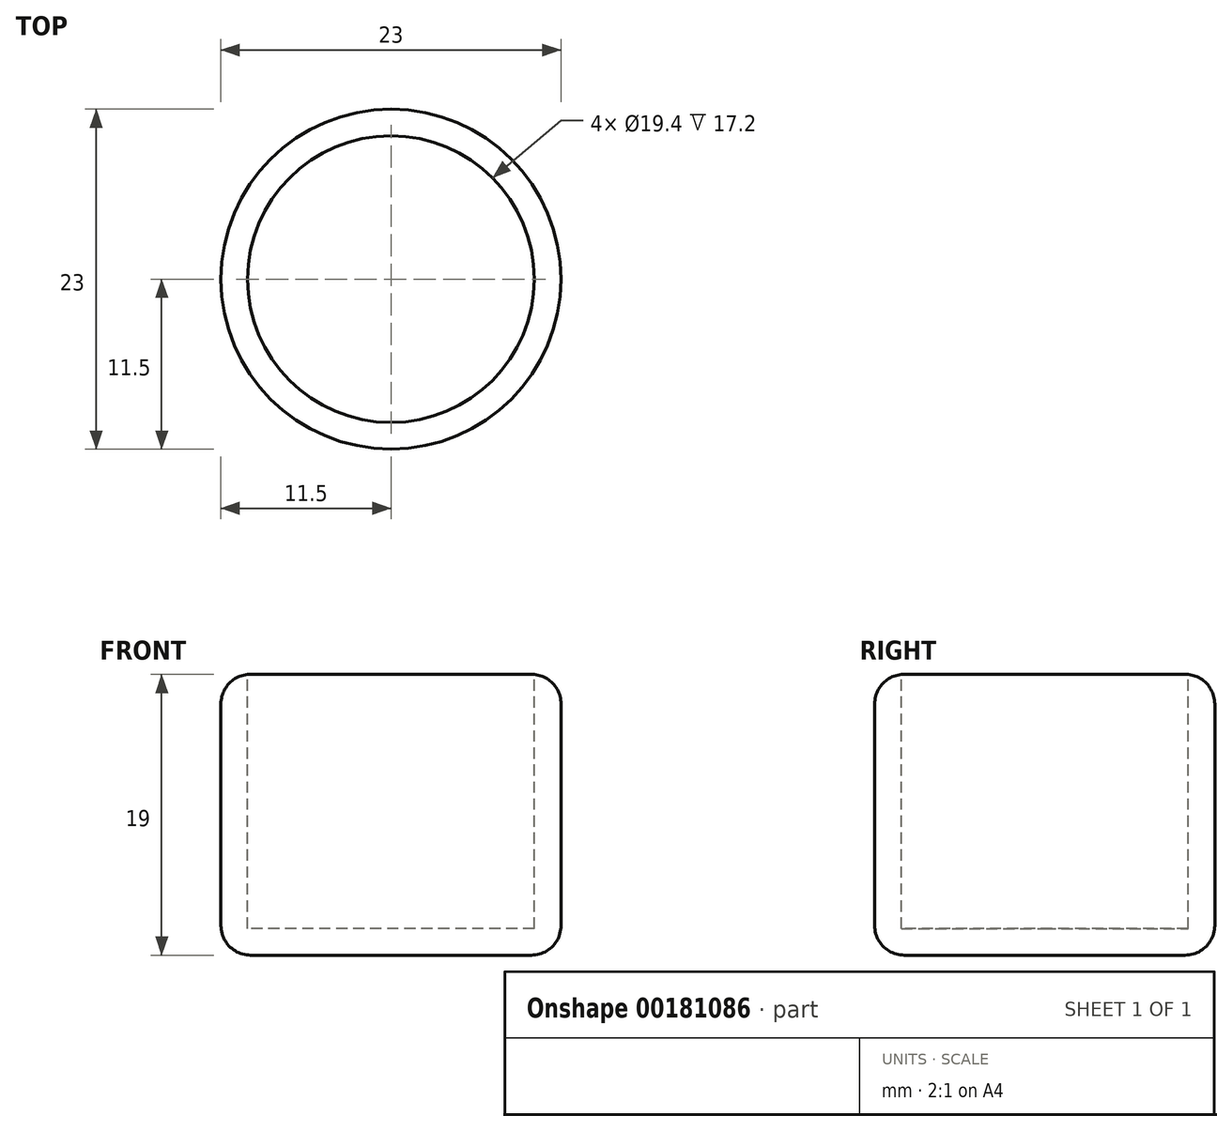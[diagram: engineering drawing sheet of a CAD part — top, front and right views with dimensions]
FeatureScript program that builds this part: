
annotation { "Feature Type Name" : "Feature", "Feature Type Description" : "" }
export const myFeature = defineFeature(function(context is Context, id is Id, definition is map)
    precondition{}
    {
        {
            var Q0;
            Q0=qCreatedBy(makeId("Top.planeOp"),FACE);
            var sketch = newSketch(context, id + "F0", { "sketchPlane" : qUnion([Q0])});
            skCircle(sketch, "E0", {"center": v(0, 0) * mm, "radius": 11.5 * mm});
            skSolve(sketch);
        }
        {
            var Q0;
            Q0=makeQuery(id+"F0.imprint","IMPRINT",FACE,{"disambiguationData":[TD([[makeQuery(id+"F0.imprint","IMPRINT",EDGE,{"derivedFrom":sQuery(id+"F0.wireOp",EDGE,"E0")}),1.0]])]});
            var Q1;
            Q1=sQuery(id+"F0.wireOp",EDGE,"E0");
            extrude(context, id + "F1", {"entities" : qUnion([Q0]), "surfaceEntities" : qUnion([Q1]), "oppositeDirection" : true, "depth" : 19 * mm});
        }
        {
            var Q0;
            Q0=makeQuery(id+"F1.opExtrude","CAP_FACE",FACE,{"disambiguationData":[OSD([sQuery(id+"F0.wireOp",EDGE,"E0")])],"isStart":true});
            shell(context, id + "F2", {"entities" : qUnion([Q0]), "thickness" : 1.8 * mm});
        }
        {
            var Q0;
            Q0=makeQuery(id+"F1.opExtrude","CAP_EDGE",EDGE,{"disambiguationData":[OSD([sQuery(id+"F0.wireOp",EDGE,"E0")])],"isStart":false});
            var Q1;
            Q1=makeQuery(id+"F1.opExtrude","CAP_EDGE",EDGE,{"disambiguationData":[OSD([sQuery(id+"F0.wireOp",EDGE,"E0")])],"isStart":true});
            fillet(context, id + "F3", {"entities" : qUnion([Q0, Q1]), "radius" : 2 * mm, "tangentPropagation" : true, "allowEdgeOverflow" : false});
        }
    });
